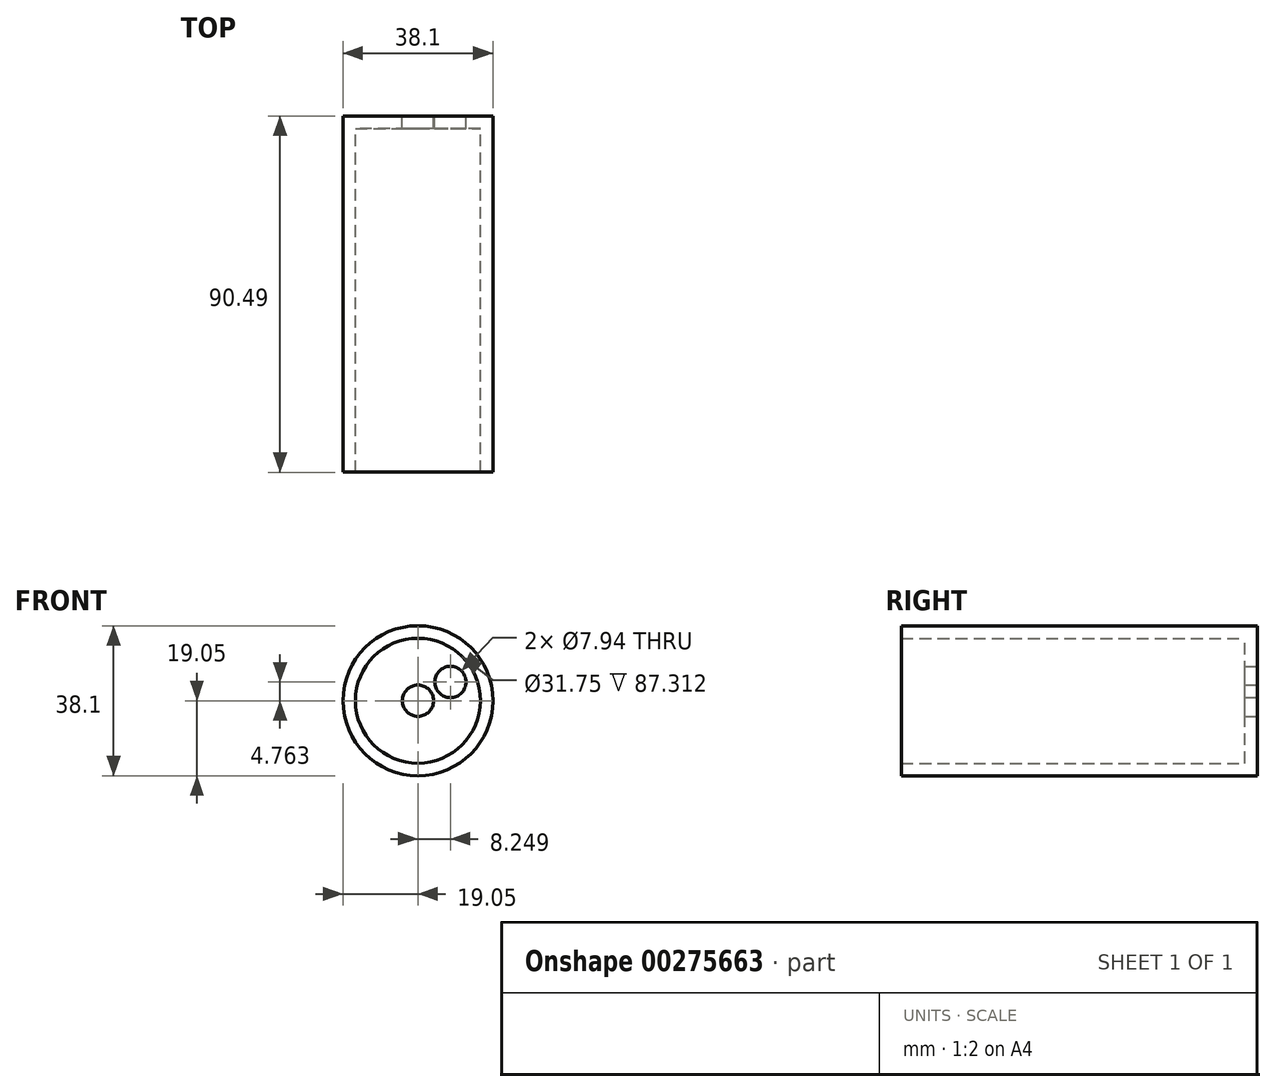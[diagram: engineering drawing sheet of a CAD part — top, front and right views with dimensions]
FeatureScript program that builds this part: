
annotation { "Feature Type Name" : "Feature", "Feature Type Description" : "" }
export const myFeature = defineFeature(function(context is Context, id is Id, definition is map)
    precondition{}
    {
        {
            var Q0;
            Q0=qCreatedBy(makeId("Front.planeOp"),FACE);
            var sketch = newSketch(context, id + "F0", { "sketchPlane" : qUnion([Q0])});
            skCircle(sketch, "E0", {"center": v(0, 0) * mm, "radius": 19.05 * mm});
            skCircle(sketch, "E1", {"center": v(0, 0) * mm, "radius": 15.88 * mm});
            skCircle(sketch, "E2", {"center": v(0, 0) * mm, "radius": 3.97 * mm});
            skLineSegment(sketch, "E3", {"start": v(-21.9, 0) * mm, "end": v(26.8, 0) * mm, "construction": true});
            skLineSegment(sketch, "E4", {"start": v(0, 0) * mm, "end": v(8.25, 4.76) * mm});
            skCircle(sketch, "E5", {"center": v(8.25, 4.76) * mm, "radius": 3.97 * mm});
            skSolve(sketch);
        }
        {
            var Q0;
            Q0 = qSketchRegion(id + "F0", true);
            extrude(context, id + "F1", {"entities" : qUnion([Q0]), "depth" : 90.49 * mm});
        }
        {
            var Q0;
            Q0=makeQuery(id+"F0.imprint","IMPRINT",FACE,{"disambiguationData":[TD([[makeQuery(id+"F0.imprint","IMPRINT",EDGE,{"derivedFrom":sQuery(id+"F0.wireOp",EDGE,"E1")}),1.0]])]});
            extrude(context, id + "F2", {"entities" : qUnion([Q0]), "operationType" : NewBodyOperationType.ADD, "depth" : 3.17 * mm});
        }
    });
